# Revit family: IS_ConceptAir_Multiproduct_BIM_GB_E0817;E0818;E0819;E0821;E0842;E0844;E0846
name_source: partatom
category: Plumbing Fixtures
revit_build: Autodesk Revit MEP 2014 (Build: 20140709_2115(x64)
units: mm (PartAtom-declared; Revit-internal decimal feet)

## types (42) — shared parameters
Accessories = www.idealspec.co.uk
AreaUnits = millimeters
Assembly Code = C1030200
AssetType = Fixed
BREEAM = No
Brand = IdealStandard
Default Elevation = 800 mm  [stored 2.62467 ft]
DurationUnit = year
ECA = No
ExpectedLife = 30
IfcExportAs = IfcFurnitureType
IfcExportType = USERDEFINED
InstallationInstructions = www.idealspec.co.uk/resources.html
LinearUnits = millimeters
ManufacturerURL = www.idealspec.co.uk
Material = Laquered MDF
NBSDescription = Bathroom integrated duct work
NBSReference = 45-35-72/320
NettWeight = 0 Kg
Shape = Rectangular
Space = Internal
SpareParts = www.fastpart-spares.co.uk
TMV3 = No
URL = www.idealspec.co.uk
Uniclass2 = Pr_40_30_78_04
Version = 1
VolumeUnits = Litres
WRAS = No
WarrantyDescription = Manufacturers warranty
WarrantyDurationParts = 5
WarrantyDurationUnit = year
WaterEfficientProduct = No
zero-valued in all types: CWFU, Cost, HWFU, WFU

## per-type parameters (varying)
| type | 1Drawer | 2Drawer | BIMObjectName | Color | Description | Features | Finish | InnerColour | MainColor | MainColour | Model | ModelNumber | ModelReference | Name | NominalDepth | NominalHeight | NominalLength | NominalWidth | ProductInformation | Size |
| E0818B2 - 60CM Wall Hung Vanity Unit 2 drawers Gls White + Matt White | No | Yes | ISI_IdealStandard_Furniture_ConceptAir_E0818B2 | White | Concept Air 60 cm Wall Hung Vanity Unit 2 Drawers Gls White + Matt White | 60 cm Wall Hung Vanity Unit 2 Drawers Gls White + Matt White | White | ISI_IdealStandard_Laminate_White_Render | White | ISI_IdealStandard_Laminate_White_Render | E0818B2 | E0818B2 | Concept Air 60 cm Wall Hung Vanity Unit 2 Drawers Gls White + Matt White | Furniture_ConceptAir_E0818B2_IdealStandard | 440 mm  [stored 1.44357 ft] | 517 mm  [stored 1.69619 ft] | 440 mm  [stored 1.44357 ft] | 600 mm | www.idealspec.co.uk/assets/datasheet/E0818B2 | 517 x 440 x 600 mm |
| E0818EQ - 60CM Wall Hung Vanity Unit 2 drawers Gls Light Grey + Matt White | No | Yes | ISI_IdealStandard_Furniture_ConceptAir_E0818EQ | Grey | Concept Air 60 cm Wall Hung Vanity Unit 2 Drawers Gls Light Grey + Matt White | 60 cm Wall Hung Vanity Unit 2 Drawers Gls Light Grey + Matt White | Grey | ISI_IdealStandard_Laminate_White_Render | Grey | ISI_IdealStandard_Furniture_Grey_Render | E0818EQ | E0818EQ | Concept Air 60 cm Wall Hung Vanity Unit 2 Drawers Gls Light Grey + Matt White | Furniture_ConceptAir_E0818EQ_IdealStandard | 440 mm  [stored 1.44357 ft] | 517 mm  [stored 1.69619 ft] | 440 mm  [stored 1.44357 ft] | 600 mm | www.idealspec.co.uk/assets/datasheet/E0818EQ | 517 x 440 x 600 mm |
| E0818KN - 60CM Wall Hung Vanity Unit 2 drawers Gls White + Matt Light Grey | No | Yes | ISI_IdealStandard_Furniture_ConceptAir_E0818KN | White | Concept Air 60 cm Wall Hung Vanity Unit 2 Drawers Gls White + Matt Light Grey | 60 cm Wall Hung Vanity Unit 2 Drawers Gls White + Matt Light Grey | White | ISI_IdealStandard_Furniture_Grey_Render | White | ISI_IdealStandard_Laminate_White_Render | E0818KN | E0818KN | Concept Air 60 cm Wall Hung Vanity Unit 2 Drawers Gls White + Matt Light Grey | Furniture_ConceptAir_E0818KN_IdealStandard | 440 mm  [stored 1.44357 ft] | 517 mm  [stored 1.69619 ft] | 440 mm  [stored 1.44357 ft] | 600 mm | www.idealspec.co.uk/assets/datasheet/E0818KN | 517 x 440 x 600 mm |
| E0818PS - 60CM Wall Hung Vanity Unit 2 drawers Wood Light Grey + Matt White | No | Yes | ISI_IdealStandard_Furniture_ConceptAir_E0818PS | Wood grey | Concept Air 60 cm Wall Hung Vanity Unit 2 Drawers Wood Light Grey + Matt White | 60 cm Wall Hung Vanity Unit 2 Drawers Wood Light Grey + Matt White | Wood grey | ISI_IdealStandard_Laminate_White_Render | Wood grey | ISI_IdealStandard_Furniture_WoodLightGrey_Render | E0818PS | E0818PS | Concept Air 60 cm Wall Hung Vanity Unit 2 Drawers Wood Light Grey + Matt White | Furniture_ConceptAir_E0818PS_IdealStandard | 440 mm  [stored 1.44357 ft] | 517 mm  [stored 1.69619 ft] | 440 mm  [stored 1.44357 ft] | 600 mm | www.idealspec.co.uk/assets/datasheet/E0818PS | 517 x 440 x 600 mm |
| E0818UK - 60CM Wall Hung Vanity Unit 2 drawers Wood Light Brown + Matt Light Brown | No | Yes | ISI_IdealStandard_Furniture_ConceptAir_E0818UK | Wood brown | Concept Air 60 cm Wall Hung Vanity Unit 2 Drawers Wood Light Brown + Matt Light Brown | 60 cm Wall Hung Vanity Unit 2 Drawers Wood Light Brown + Matt Light Brown | Wood brown | ISI_IdealStandard_Furniture_WoodLightBrown_Render | Wood brown | ISI_IdealStandard_Furniture_WoodLightBrown_Render | E0818UK | E0818UK | Concept Air 60 cm Wall Hung Vanity Unit 2 Drawers Wood Light Brown + Matt Light Brown | Furniture_ConceptAir_E0818UK_IdealStandard | 440 mm  [stored 1.44357 ft] | 517 mm  [stored 1.69619 ft] | 440 mm  [stored 1.44357 ft] | 600 mm | www.idealspec.co.uk/assets/datasheet/E0818UK | 517 x 440 x 600 mm |
| E0819B2 - 80CM Wall Hung Vanity Unit 2 drawers Gls White + Matt White | No | Yes | ISI_IdealStandard_Furniture_ConceptAir_E0819B2 | White | Concept Air 80 cm Wall Hung Vanity Unit 2 Drawers Gls White + Matt White | 80 cm Wall Hung Vanity Unit 2 Drawers Gls White + Matt White | White | ISI_IdealStandard_Laminate_White_Render | White | ISI_IdealStandard_Laminate_White_Render | E0819B2 | E0819B2 | Concept Air 80 cm Wall Hung Vanity Unit 2 Drawers Gls White + Matt White | Furniture_ConceptAir_E0819B2_IdealStandard | 440 mm  [stored 1.44357 ft] | 517 mm  [stored 1.69619 ft] | 440 mm  [stored 1.44357 ft] | 800 mm  [stored 2.62467 ft] | www.idealspec.co.uk/assets/datasheet/E0819B2 | 517 x 440 x 800 mm |
| E0821EQ - 100CM Wall Hung Vanity Unit 2 drawers Gls Light Grey + Matt White | No | Yes | ISI_IdealStandard_Furniture_ConceptAir_E0821EQ | Grey | Concept Air 100 cm Wall Hung Vanity Unit 2 Drawers Gls Light Grey + Matt White | 100 cm Wall Hung Vanity Unit 2 Drawers Gls Light Grey + Matt White | Grey | ISI_IdealStandard_Laminate_White_Render | Grey | ISI_IdealStandard_Furniture_Grey_Render | E0821EQ | E0821EQ | Concept Air 100 cm Wall Hung Vanity Unit 2 Drawers Gls Light Grey + Matt White | Furniture_ConceptAir_E0821EQ_IdealStandard | 440 mm  [stored 1.44357 ft] | 517 mm  [stored 1.69619 ft] | 440 mm  [stored 1.44357 ft] | 1000 mm  [stored 3.28084 ft] | www.idealspec.co.uk/assets/datasheet/E0821EQ | 517 x 440 x 1000 mm |
| E0819KN - 80CM Wall Hung Vanity Unit 2 drawers Gls White + Matt Light Grey | No | Yes | ISI_IdealStandard_Furniture_ConceptAir_E0819KN | White | Concept Air 80 cm Wall Hung Vanity Unit 2 Drawers Gls White + Matt Light Grey | 80 cm Wall Hung Vanity Unit 2 Drawers Gls White + Matt Light Grey | White | ISI_IdealStandard_Furniture_Grey_Render | White | ISI_IdealStandard_Laminate_White_Render | E0819KN | E0819KN | Concept Air 80 cm Wall Hung Vanity Unit 2 Drawers Gls White + Matt Light Grey | Furniture_ConceptAir_E0819KN_IdealStandard | 440 mm  [stored 1.44357 ft] | 517 mm  [stored 1.69619 ft] | 440 mm  [stored 1.44357 ft] | 800 mm  [stored 2.62467 ft] | www.idealspec.co.uk/assets/datasheet/E0819KN | 517 x 440 x 800 mm |
| E0819PS - 80CM Wall Hung Vanity Unit 2 drawers Wood Light Grey + Matt White | No | Yes | ISI_IdealStandard_Furniture_ConceptAir_E0819PS | Wood grey | Concept Air 80 cm Wall Hung Vanity Unit 2 Drawers Wood Light Grey + Matt White | 80 cm Wall Hung Vanity Unit 2 Drawers Wood Light Grey + Matt White | Wood grey | ISI_IdealStandard_Laminate_White_Render | Wood grey | ISI_IdealStandard_Furniture_WoodLightGrey_Render | E0819PS | E0819PS | Concept Air 80 cm Wall Hung Vanity Unit 2 Drawers Wood Light Grey + Matt White | Furniture_ConceptAir_E0819PS_IdealStandard | 440 mm  [stored 1.44357 ft] | 517 mm  [stored 1.69619 ft] | 440 mm  [stored 1.44357 ft] | 800 mm  [stored 2.62467 ft] | www.idealspec.co.uk/assets/datasheet/E0819PS | 517 x 440 x 800 mm |
| E0819UK - 80CM Wall Hung Vanity Unit 2 drawers Wood Light Brown + Matt Light Brown | No | Yes | ISI_IdealStandard_Furniture_ConceptAir_E0819UK | Wood brown | Concept Air 80 cm Wall Hung Vanity Unit 2 Drawers Wood Light Brown + Matt Light Brown | 80 cm Wall Hung Vanity Unit 2 Drawers Wood Light Brown + Matt Light Brown | Wood brown | ISI_IdealStandard_Furniture_WoodLightBrown_Render | Wood brown | ISI_IdealStandard_Furniture_WoodLightBrown_Render | E0819UK | E0819UK | Concept Air 80 cm Wall Hung Vanity Unit 2 Drawers Wood Light Brown + Matt Light Brown | Furniture_ConceptAir_E0819UK_IdealStandard | 440 mm  [stored 1.44357 ft] | 517 mm  [stored 1.69619 ft] | 440 mm  [stored 1.44357 ft] | 800 mm  [stored 2.62467 ft] | www.idealspec.co.uk/assets/datasheet/E0819UK | 517 x 440 x 800 mm |
| E0819EQ - 80CM Wall Hung Vanity Unit 2 drawers Gls Light Grey + Matt White | No | Yes | ISI_IdealStandard_Furniture_ConceptAir_E0819EQ | Grey | Concept Air 80 cm Wall Hung Vanity Unit 2 Drawers Gls Light Grey + Matt White | 80 cm Wall Hung Vanity Unit 2 Drawers Gls Light Grey + Matt White | Grey | ISI_IdealStandard_Laminate_White_Render | Grey | ISI_IdealStandard_Furniture_Grey_Render | E0819EQ | E0819EQ | Concept Air 80 cm Wall Hung Vanity Unit 2 Drawers Gls Light Grey + Matt White | Furniture_ConceptAir_E0819EQ_IdealStandard | 440 mm  [stored 1.44357 ft] | 517 mm  [stored 1.69619 ft] | 440 mm  [stored 1.44357 ft] | 800 mm  [stored 2.62467 ft] | www.idealspec.co.uk/assets/datasheet/E0819EQ | 517 x 440 x 800 mm |
| E0821KN - 100CM Wall Hung Vanity Unit 2 drawers Gls White + Matt Light Grey | No | Yes | ISI_IdealStandard_Furniture_ConceptAir_E0821KN | White | Concept Air 100 cm Wall Hung Vanity Unit 2 Drawers Gls White + Matt Light Grey | 100 cm Wall Hung Vanity Unit 2 Drawers Gls White + Matt Light Grey | White | ISI_IdealStandard_Furniture_Grey_Render | White | ISI_IdealStandard_Laminate_White_Render | E0821KN | E0821KN | Concept Air 100 cm Wall Hung Vanity Unit 2 Drawers Gls White + Matt Light Grey | Furniture_ConceptAir_E0821KN_IdealStandard | 440 mm  [stored 1.44357 ft] | 517 mm  [stored 1.69619 ft] | 440 mm  [stored 1.44357 ft] | 1000 mm  [stored 3.28084 ft] | www.idealspec.co.uk/assets/datasheet/E0821KN | 517 x 440 x 1000 mm |
| E0821PS - 100CM Wall Hung Vanity Unit 2 drawers Wood Light Grey + Matt White | No | Yes | ISI_IdealStandard_Furniture_ConceptAir_E0821PS | Wood grey | Concept Air 100 cm Wall Hung Vanity Unit 2 Drawers Wood Light Grey + Matt White | 100 cm Wall Hung Vanity Unit 2 Drawers Wood Light Grey + Matt White | Wood grey | ISI_IdealStandard_Laminate_White_Render | Wood grey | ISI_IdealStandard_Furniture_WoodLightGrey_Render | E0821PS | E0821PS | Concept Air 100 cm Wall Hung Vanity Unit 2 Drawers Wood Light Grey + Matt White | Furniture_ConceptAir_E0821PS_IdealStandard | 440 mm  [stored 1.44357 ft] | 517 mm  [stored 1.69619 ft] | 440 mm  [stored 1.44357 ft] | 1000 mm  [stored 3.28084 ft] | www.idealspec.co.uk/assets/datasheet/E0821PS | 517 x 440 x 1000 mm |
| E0821UK - 100CM Wall Hung Vanity Unit 2 drawers Wood Light Brown + Matt Light Brown | No | Yes | ISI_IdealStandard_Furniture_ConceptAir_E0821UK | Wood brown | Concept Air 100 cm Wall Hung Vanity Unit 2 Drawers Wood Light Brown + Matt Light Brown | 100 cm Wall Hung Vanity Unit 2 Drawers Wood Light Brown + Matt Light Brown | Wood brown | ISI_IdealStandard_Furniture_WoodLightBrown_Render | Wood brown | ISI_IdealStandard_Furniture_WoodLightBrown_Render | E0821UK | E0821UK | Concept Air 100 cm Wall Hung Vanity Unit 2 Drawers Wood Light Brown + Matt Light Brown | Furniture_ConceptAir_E0821UK_IdealStandard | 440 mm  [stored 1.44357 ft] | 517 mm  [stored 1.69619 ft] | 440 mm  [stored 1.44357 ft] | 1000 mm  [stored 3.28084 ft] | www.idealspec.co.uk/assets/datasheet/E0821UK | 517 x 440 x 1000 mm |
| E0821B2 - 100CM Wall Hung Vanity Unit 2 drawers Gls White + Matt White | No | Yes | ISI_IdealStandard_Furniture_ConceptAir_E0821B2 | White | Concept Air 100 cm Wall Hung Vanity Unit 2 Drawers Gls White + Matt White | 100 cm Wall Hung Vanity Unit 2 Drawers Gls White + Matt White | White | ISI_IdealStandard_Laminate_White_Render | White | ISI_IdealStandard_Laminate_White_Render | E0821B2 | E0821B2 | Concept Air 100 cm Wall Hung Vanity Unit 2 Drawers Gls White + Matt White | Furniture_ConceptAir_E0821B2_IdealStandard | 440 mm  [stored 1.44357 ft] | 517 mm  [stored 1.69619 ft] | 440 mm  [stored 1.44357 ft] | 1000 mm  [stored 3.28084 ft] | www.idealspec.co.uk/assets/datasheet/E0821B2 | 517 x 440 x 1000 mm |
| E0817B2 - 50CM Wall Hung Vanity Unit 1 drawer Gls White + Matt White | Yes | No | ISI_IdealStandard_Furniture_ConceptAir_E0817B2 | White | Concept Air 50 cm Wall Hung Vanity Unit 1 Drawer Gls White + Matt White | 50 cm Wall Hung Vanity Unit 1 Drawer Gls White + Matt White | White | ISI_IdealStandard_Laminate_White_Render | White | ISI_IdealStandard_Laminate_White_Render | E0817B2 | E0817B2 | Concept Air 50 cm Wall Hung Vanity Unit 1 Drawer Gls White + Matt White | Furniture_ConceptAir_E0817B2_IdealStandard | 360 mm  [stored 1.1811 ft] | 400 mm  [stored 1.31234 ft] | 360 mm  [stored 1.1811 ft] | 500 mm  [stored 1.64042 ft] | www.idealspec.co.uk/assets/datasheet/E0817B2 | 400 x 360 x 500 mm |
| E0817EQ - 50CM Wall Hung Vanity Unit 1 drawer Gls Light Grey + Matt White | Yes | No | ISI_IdealStandard_Furniture_ConceptAir_E0817EQ | Grey | Concept Air 50 cm Wall Hung Vanity Unit 1 Drawer Gls Light Grey + Matt White | 50 cm Wall Hung Vanity Unit 1 Drawer Gls White + Matt White | Grey | ISI_IdealStandard_Laminate_White_Render | Grey | ISI_IdealStandard_Furniture_Grey_Render | E0817EQ | E0817EQ | Concept Air 50 cm Wall Hung Vanity Unit 1 Drawer Gls Light Grey + Matt White | Furniture_ConceptAir_E0817EQ_IdealStandard | 360 mm  [stored 1.1811 ft] | 400 mm  [stored 1.31234 ft] | 360 mm  [stored 1.1811 ft] | 500 mm  [stored 1.64042 ft] | www.idealspec.co.uk/assets/datasheet/E0817EQ | 400 x 360 x 500 mm |
| E0817KN - 50CM Wall Hung Vanity Unit 1 drawer Gls White + Matt Light Grey | Yes | No | ISI_IdealStandard_Furniture_ConceptAir_E0817KN | White | Concept Air 50 cm Wall Hung Vanity Unit 1 Drawer Gls White + Matt Light Grey | 50 cm Wall Hung Vanity Unit 1 Drawer Gls White + Matt White | White | ISI_IdealStandard_Furniture_Grey_Render | White | ISI_IdealStandard_Laminate_White_Render | E0817KN | E0817KN | Concept Air 50 cm Wall Hung Vanity Unit 1 Drawer Gls White + Matt Light Grey | Furniture_ConceptAir_E0817KN_IdealStandard | 360 mm  [stored 1.1811 ft] | 400 mm  [stored 1.31234 ft] | 360 mm  [stored 1.1811 ft] | 500 mm  [stored 1.64042 ft] | www.idealspec.co.uk/assets/datasheet/E0817KN | 400 x 360 x 500 mm |
| E0817PS - 50CM Wall Hung Vanity Unit 1 drawer Wood Light Grey + Matt White | Yes | No | ISI_IdealStandard_Furniture_ConceptAir_E0817PS | Wood grey | Concept Air 50 cm Wall Hung Vanity Unit 1 Drawer Wood Light Grey + Matt White | 50 cm Wall Hung Vanity Unit 1 Drawer Wood Light Grey + Matt White | Wood grey | ISI_IdealStandard_Laminate_White_Render | Wood grey | ISI_IdealStandard_Furniture_WoodLightGrey_Render | E0817PS | E0817PS | Concept Air 50 cm Wall Hung Vanity Unit 1 Drawer Wood Light Grey + Matt White | Furniture_ConceptAir_E0817PS_IdealStandard | 360 mm  [stored 1.1811 ft] | 400 mm  [stored 1.31234 ft] | 360 mm  [stored 1.1811 ft] | 500 mm  [stored 1.64042 ft] | www.idealspec.co.uk/assets/datasheet/E0817PS | 400 x 360 x 500 mm |
| E0817UK - 50CM Wall Hung Vanity Unit 1 drawer Wood Light Brown + Matt Light Brown | Yes | No | ISI_IdealStandard_Furniture_ConceptAir_E0817UK | Wood brown | Concept Air 50 cm Wall Hung Vanity Unit 1 Drawer Wood Light Brown + Matt Light Brown | 50 cm Wall Hung Vanity Unit 1 Drawer Wood Light Brown + Matt Light Brown | Wood brown | ISI_IdealStandard_Furniture_WoodLightBrown_Render | Wood brown | ISI_IdealStandard_Furniture_WoodLightBrown_Render | E0817UK | E0817UK | Concept Air 50 cm Wall Hung Vanity Unit 1 Drawer Wood Light Brown + Matt Light Brown | Furniture_ConceptAir_E0817UK_IdealStandard | 360 mm  [stored 1.1811 ft] | 400 mm  [stored 1.31234 ft] | 360 mm  [stored 1.1811 ft] | 500 mm  [stored 1.64042 ft] | www.idealspec.co.uk/assets/datasheet/E0817UK | 400 x 360 x 500 mm |
| E0842B2 - 44CM Cube WH Vanity unit 1 drawer Gls White + Matt White | Yes | No | ISI_IdealStandard_Furniture_ConceptAir_E0842B2 | White | Concept Air 50 cm Cube Wh Vanity Unit 1 Drawer Gls White + Matt White | 50 cm Cube Wh Vanity Unit 1 Drawer Gls White + Matt White | White | ISI_IdealStandard_Laminate_White_Render | White | ISI_IdealStandard_Laminate_White_Render | E0842B2 | E0842B2 | Concept Air 44 cm Cube Wh Vanity Unit 1 Drawer Gls White + Matt White | Furniture_ConceptAir_E0842B2_IdealStandard | 412 mm  [stored 1.35171 ft] | 400 mm  [stored 1.31234 ft] | 412 mm  [stored 1.35171 ft] | 435 mm  [stored 1.42717 ft] | www.idealspec.co.uk/assets/datasheet/E0842B2 | 400 x 412 x 435 mm |
| E0842EQ - 44CM Cube WH Vanity unit 1 drawer Gls Light Grey + Matt White | Yes | No | ISI_IdealStandard_Furniture_ConceptAir_E0842EQ | Grey | Concept Air 50 cm Cube Wh Vanity Unit 1 Drawer Gls Light Grey + Matt White | 50 cm Cube Wh Vanity Unit 1 Drawer Gls Light Grey + Matt White | Grey | ISI_IdealStandard_Laminate_White_Render | Grey | ISI_IdealStandard_Furniture_Grey_Render | E0842EQ | E0842EQ | Concept Air 44 cm Cube Wh Vanity Unit 1 Drawer Gls Light Grey + Matt White | Furniture_ConceptAir_E0842EQ_IdealStandard | 412 mm  [stored 1.35171 ft] | 400 mm  [stored 1.31234 ft] | 412 mm  [stored 1.35171 ft] | 435 mm  [stored 1.42717 ft] | www.idealspec.co.uk/assets/datasheet/E0842EQ | 400 x 412 x 435 mm |
| E0842KN - 44CM Cube WH Vanity unit 1 drawer Gls White + Matt Light Grey | Yes | No | ISI_IdealStandard_Furniture_ConceptAir_E0842KN | White | Concept Air 50 cm Cube Wh Vanity Unit 1 Drawer Gls White + Matt Light Grey | 50 cm Cube Wh Vanity Unit 1 Drawer Gls White + Matt Light Grey | White | ISI_IdealStandard_Furniture_Grey_Render | White | ISI_IdealStandard_Laminate_White_Render | E0842KN | E0842KN | Concept Air 44 cm Cube Wh Vanity Unit 1 Drawer Gls White + Matt Light Grey | Furniture_ConceptAir_E0842KN_IdealStandard | 412 mm  [stored 1.35171 ft] | 400 mm  [stored 1.31234 ft] | 412 mm  [stored 1.35171 ft] | 435 mm  [stored 1.42717 ft] | www.idealspec.co.uk/assets/datasheet/E0842KN | 400 x 412 x 435 mm |
| E0842PS - 44CM Cube WH Vanity unit 1 drawer Wood Light Grey + Matt White | Yes | No | ISI_IdealStandard_Furniture_ConceptAir_E0842PS | Wood grey | Concept Air 50 cm Cube Wh Vanity Unit 1 Drawer Wood Light Grey + Matt White | 50 cm Cube Wh Vanity Unit 1 Drawer Wood Light Grey + Matt White | Wood grey | ISI_IdealStandard_Laminate_White_Render | Wood grey | ISI_IdealStandard_Furniture_WoodLightGrey_Render | E0842PS | E0842PS | Concept Air 44 cm Cube Wh Vanity Unit 1 Drawer Wood Light Grey + Matt White | Furniture_ConceptAir_E0842PS_IdealStandard | 412 mm  [stored 1.35171 ft] | 400 mm  [stored 1.31234 ft] | 412 mm  [stored 1.35171 ft] | 435 mm  [stored 1.42717 ft] | www.idealspec.co.uk/assets/datasheet/E0842PS | 400 x 412 x 435 mm |
| E0842UK - 44CM Cube WH Vanity unit 1 drawer Wood Light Brown + Matt Light Brown | Yes | No | ISI_IdealStandard_Furniture_ConceptAir_E0842UK | Wood brown | Concept Air 50 cm Cube Wh Vanity Unit 1 Drawer Wood Light Brown + Matt Light Brown | 50 cm Cube Wh Vanity Unit 1 Drawer Wood Light Brown + Matt Light Brown | Wood brown | ISI_IdealStandard_Furniture_WoodLightBrown_Render | Wood brown | ISI_IdealStandard_Furniture_WoodLightBrown_Render | E0842UK | E0842UK | Concept Air 44 cm Cube Wh Vanity Unit 1 Drawer Wood Light Brown + Matt Light Brown | Furniture_ConceptAir_E0842UK_IdealStandard | 412 mm  [stored 1.35171 ft] | 400 mm  [stored 1.31234 ft] | 412 mm  [stored 1.35171 ft] | 435 mm  [stored 1.42717 ft] | www.idealspec.co.uk/assets/datasheet/E0842UK | 400 x 412 x 435 mm |
| E0844B2 - 48CM Cube WH Vanity unit 1 drawer Gls White + Matt White | Yes | No | ISI_IdealStandard_Furniture_ConceptAir_E0844B2 | White | Concept Air 55 cm Cube Wh Vanity Unit 1 Drawer Gls White + Matt White | 55 cm Cube Wh Vanity Unit 1 Drawer Gls White + Matt White | White | ISI_IdealStandard_Laminate_White_Render | White | ISI_IdealStandard_Laminate_White_Render | E0844B2 | E0844B2 | Concept Air 48 cm Cube Wh Vanity Unit 1 Drawer Gls White + Matt White | Furniture_ConceptAir_E0844B2_IdealStandard | 412 mm  [stored 1.35171 ft] | 400 mm  [stored 1.31234 ft] | 412 mm  [stored 1.35171 ft] | 485 mm  [stored 1.59121 ft] | www.idealspec.co.uk/assets/datasheet/E0844B2 | 400 x 412 x 485 mm |
| E0844EQ - 48CM Cube WH Vanity unit 1 drawer Gls Light Grey + Matt White | Yes | No | ISI_IdealStandard_Furniture_ConceptAir_E0844EQ | Grey | Concept Air 55 cm Cube Wh Vanity Unit 1 Drawer Gls Light Grey + Matt White | 55 cm Cube Wh Vanity Unit 1 Drawer Gls Light Grey + Matt White | Grey | ISI_IdealStandard_Laminate_White_Render | Grey | ISI_IdealStandard_Furniture_Grey_Render | E0844EQ | E0844EQ | Concept Air 48 cm Cube Wh Vanity Unit 1 Drawer Gls Light Grey + Matt White | Furniture_ConceptAir_E0844EQ_IdealStandard | 412 mm  [stored 1.35171 ft] | 400 mm  [stored 1.31234 ft] | 412 mm  [stored 1.35171 ft] | 485 mm  [stored 1.59121 ft] | www.idealspec.co.uk/assets/datasheet/E0844EQ | 400 x 412 x 485 mm |
| E0844KN - 48CM Cube WH Vanity unit 1 drawer Gls White + Matt Light Grey | Yes | No | ISI_IdealStandard_Furniture_ConceptAir_E0844KN | White | Concept Air 55 cm Cube Wh Vanity Unit 1 Drawer Gls White + Matt Light Grey | 55 cm Cube Wh Vanity Unit 1 Drawer Gls White + Matt Light Grey | White | ISI_IdealStandard_Furniture_Grey_Render | White | ISI_IdealStandard_Laminate_White_Render | E0844KN | E0844KN | Concept Air 48 cm Cube Wh Vanity Unit 1 Drawer Gls White + Matt Light Grey | Furniture_ConceptAir_E0844KN_IdealStandard | 412 mm  [stored 1.35171 ft] | 400 mm  [stored 1.31234 ft] | 412 mm  [stored 1.35171 ft] | 485 mm  [stored 1.59121 ft] | www.idealspec.co.uk/assets/datasheet/E0844KN | 400 x 412 x 485 mm |
| E0844PS - 48CM Cube WH Vanity unit 1 drawer Wood Light Grey + Matt White | Yes | No | ISI_IdealStandard_Furniture_ConceptAir_E0844PS | Wood grey | Concept Air 55 cm Cube Wh Vanity Unit 1 Drawer Wood Light Grey + Matt White | 55 cm Cube Wh Vanity Unit 1 Drawer Wood Light Grey + Matt White | Wood grey | ISI_IdealStandard_Laminate_White_Render | Wood grey | ISI_IdealStandard_Furniture_WoodLightGrey_Render | E0844PS | E0844PS | Concept Air 48 cm Cube Wh Vanity Unit 1 Drawer Wood Light Grey + Matt White | Furniture_ConceptAir_E0844PS_IdealStandard | 412 mm  [stored 1.35171 ft] | 400 mm  [stored 1.31234 ft] | 412 mm  [stored 1.35171 ft] | 485 mm  [stored 1.59121 ft] | www.idealspec.co.uk/assets/datasheet/E0844PS | 400 x 412 x 485 mm |
| E0844UK - 48CM Cube WH Vanity unit 1 drawer Wood Light Brown + Matt Light Brown | Yes | No | ISI_IdealStandard_Furniture_ConceptAir_E0844UK | Wood brown | Concept Air 55 cm Cube Wh Vanity Unit 1 Drawer Wood Light Brown + Matt Light Brown | 55 cm Cube Wh Vanity Unit 1 Drawer Wood Light Brown + Matt Light Brown | Wood brown | ISI_IdealStandard_Furniture_WoodLightBrown_Render | Wood brown | ISI_IdealStandard_Furniture_WoodLightBrown_Render | E0844UK | E0844UK | Concept Air 48 cm Cube Wh Vanity Unit 1 Drawer Wood Light Brown + Matt Light Brown | Furniture_ConceptAir_E0844UK_IdealStandard | 412 mm  [stored 1.35171 ft] | 400 mm  [stored 1.31234 ft] | 412 mm  [stored 1.35171 ft] | 485 mm  [stored 1.59121 ft] | www.idealspec.co.uk/assets/datasheet/E0844UK | 400 x 412 x 485 mm |
| E0846B2 - 54CM Cube WH Vanity unit 1 drawer Gls White + Matt White | Yes | No | ISI_IdealStandard_Furniture_ConceptAir_E0846B2 | White | Concept Air 60 cm Cube Wh Vanity Unit 1 Drawer Gls White + Matt White | 60 cm Cube Wh Vanity Unit 1 Drawer Gls White + Matt White | White | ISI_IdealStandard_Laminate_White_Render | White | ISI_IdealStandard_Laminate_White_Render | E0846B2 | E0846B2 | Concept Air 54 cm Cube Wh Vanity Unit 1 Drawer Gls White + Matt White | Furniture_ConceptAir_E0846B2_IdealStandard | 412 mm  [stored 1.35171 ft] | 400 mm  [stored 1.31234 ft] | 412 mm  [stored 1.35171 ft] | 535 mm  [stored 1.75525 ft] | www.idealspec.co.uk/assets/datasheet/E0846B2 | 400 x 412 x 535 mm |
| E0846EQ - 54CM Cube WH Vanity unit 1 drawer Gls Light Grey + Matt White | Yes | No | ISI_IdealStandard_Furniture_ConceptAir_E0846EQ | Grey | Concept Air 60 cm Cube Wh Vanity Unit 1 Drawer Gls Light Grey + Matt White | 60 cm Cube Wh Vanity Unit 1 Drawer Gls Light Grey + Matt White | Grey | ISI_IdealStandard_Laminate_White_Render | Grey | ISI_IdealStandard_Furniture_Grey_Render | E0846EQ | E0846EQ | Concept Air 54 cm Cube Wh Vanity Unit 1 Drawer Gls Light Grey + Matt White | Furniture_ConceptAir_E0846EQ_IdealStandard | 412 mm  [stored 1.35171 ft] | 400 mm  [stored 1.31234 ft] | 412 mm  [stored 1.35171 ft] | 535 mm  [stored 1.75525 ft] | www.idealspec.co.uk/assets/datasheet/E0846EQ | 400 x 412 x 535 mm |
| E0846KN - 54CM Cube WH Vanity unit 1 drawer Gls White + Matt Light Grey | Yes | No | ISI_IdealStandard_Furniture_ConceptAir_E0846KN | White | Concept Air 60 cm Cube Wh Vanity Unit 1 Drawer Gls White + Matt Light Grey | 60 cm Cube Wh Vanity Unit 1 Drawer Gls White + Matt Light Grey | White | ISI_IdealStandard_Furniture_Grey_Render | White | ISI_IdealStandard_Laminate_White_Render | E0846KN | E0846KN | Concept Air 54 cm Cube Wh Vanity Unit 1 Drawer Gls White + Matt Light Grey | Furniture_ConceptAir_E0846KN_IdealStandard | 412 mm  [stored 1.35171 ft] | 400 mm  [stored 1.31234 ft] | 412 mm  [stored 1.35171 ft] | 535 mm  [stored 1.75525 ft] | www.idealspec.co.uk/assets/datasheet/E0846KN | 400 x 412 x 535 mm |
| E0846PS - 54CM Cube WH Vanity unit 1 drawer Wood Light Grey + Matt White | Yes | No | ISI_IdealStandard_Furniture_ConceptAir_E0846PS | Wood grey | Concept Air 60 cm Cube Wh Vanity Unit 1 Drawer Wood Light Grey + Matt White | 60 cm Cube Wh Vanity Unit 1 Drawer Wood Light Grey + Matt White | Wood grey | ISI_IdealStandard_Laminate_White_Render | Wood grey | ISI_IdealStandard_Furniture_WoodLightGrey_Render | E0846PS | E0846PS | Concept Air 54 cm Cube Wh Vanity Unit 1 Drawer Wood Light Grey + Matt White | Furniture_ConceptAir_E0846PS_IdealStandard | 412 mm  [stored 1.35171 ft] | 400 mm  [stored 1.31234 ft] | 412 mm  [stored 1.35171 ft] | 535 mm  [stored 1.75525 ft] | www.idealspec.co.uk/assets/datasheet/E0846PS | 400 x 412 x 535 mm |
| E0846UK - 54CM Cube WH Vanity unit 1 drawer Wood Light Brown + Matt Light Brown | Yes | No | ISI_IdealStandard_Furniture_ConceptAir_E0846UK | Wood brown | Concept Air 60 cm Cube Wh Vanity Unit 1 Drawer Wood Light Brown + Matt Light Brown | 60 cm Cube Wh Vanity Unit 1 Drawer Wood Light Brown + Matt Light Brown | Wood brown | ISI_IdealStandard_Furniture_WoodLightBrown_Render | Wood brown | ISI_IdealStandard_Furniture_WoodLightBrown_Render | E0846UK | E0846UK | Concept Air 54 cm Cube Wh Vanity Unit 1 Drawer Wood Light Brown + Matt Light Brown | Furniture_ConceptAir_E0846UK_IdealStandard | 412 mm  [stored 1.35171 ft] | 400 mm  [stored 1.31234 ft] | 412 mm  [stored 1.35171 ft] | 535 mm  [stored 1.75525 ft] | www.idealspec.co.uk/assets/datasheet/E0846UK | 400 x 412 x 535 mm |
| E0846VY - 54CM Cube WH Vanity unit 1 drawer Matt Dark Brown + Matt White | Yes | No | ISI_IdealStandard_Furniture_ConceptAir_E0846VY | Dark brown | Concept Air 60 cm Cube Wh Vanity Unit 1 Drawer Matt Dark Brown + Matt White | 60 cm Cube Wh Vanity Unit 1 Drawer Matt Dark Brown + Matt White | Dark brown | ISI_IdealStandard_Laminate_White_Render | Dark brown | ISI_IdealStandard_Furniture_DarkBrown_Render | E0846VY | E0846VY | Concept Air 54 cm Cube Wh Vanity Unit 1 Drawer Gls Dark Brown + Matt White | Furniture_ConceptAir_E0846VY_IdealStandard | 412 mm  [stored 1.35171 ft] | 400 mm  [stored 1.31234 ft] | 412 mm  [stored 1.35171 ft] | 535 mm  [stored 1.75525 ft] | www.idealspec.co.uk/assets/datasheet/E0846VY | 400 x 412 x 535 mm |
| E0844VY - 48CM Cube WH Vanity unit 1 drawer Matt Dark Brown + Matt White | Yes | No | ISI_IdealStandard_Furniture_ConceptAir_E0844VY | Dark brown | Concept Air 55 cm Cube Wh Vanity Unit 1 Drawer Matt Dark Brown + Matt White | 55 cm Cube Wh Vanity Unit 1 Drawer Matt Dark Brown + Matt White | Dark brown | ISI_IdealStandard_Laminate_White_Render | Dark brown | ISI_IdealStandard_Furniture_DarkBrown_Render | E0844VY | E0844VY | Concept Air 48 cm Cube Wh Vanity Unit 1 Drawer Gls Dark Brown + Matt White | Furniture_ConceptAir_E0844VY_IdealStandard | 412 mm  [stored 1.35171 ft] | 400 mm  [stored 1.31234 ft] | 412 mm  [stored 1.35171 ft] | 485 mm  [stored 1.59121 ft] | www.idealspec.co.uk/assets/datasheet/E0844VY | 400 x 412 x 485 mm |
| E0842VY - 44CM Cube WH Vanity unit 1 drawer Matt Dark Brown + Matt White | Yes | No | ISI_IdealStandard_Furniture_ConceptAir_E0842VY | Dark brown | Concept Air 50 cm Cube Wh Vanity Unit 1 Drawer Matt Dark Brown + Matt White | 50 cm Cube Wh Vanity Unit 1 Drawer Matt Dark Brown + Matt White | Dark brown | ISI_IdealStandard_Laminate_White_Render | Dark brown | ISI_IdealStandard_Furniture_DarkBrown_Render | E0842VY | E0842VY | Concept Air 44 cm Cube Wh Vanity Unit 1 Drawer Gls Dark Brown + Matt White | Furniture_ConceptAir_E0842VY_IdealStandard | 412 mm  [stored 1.35171 ft] | 400 mm  [stored 1.31234 ft] | 412 mm  [stored 1.35171 ft] | 435 mm  [stored 1.42717 ft] | www.idealspec.co.uk/assets/datasheet/E0842VY | 400 x 412 x 435 mm |
| E0817VY - 50CM Wall Hung Vanity Unit 1 drawer Matt Dark Brown + Matt White | Yes | No | ISI_IdealStandard_Furniture_ConceptAir_E0817VY | Dark brown | Concept Air 50 cm Wall Hung Vanity Unit 1 Drawer Matt Dark Brown + Matt White | 50 cm Wall Hung Vanity Unit 1 Drawer Matt Dark Brown + Matt White | Dark brown | ISI_IdealStandard_Laminate_White_Render | Dark brown | ISI_IdealStandard_Furniture_DarkBrown_Render | E0817VY | E0817VY | Concept Air 50 cm Wall Hung Vanity Unit 1 Drawer Gls Dark Brown + Matt White | Furniture_ConceptAir_E0817VY_IdealStandard | 360 mm  [stored 1.1811 ft] | 400 mm  [stored 1.31234 ft] | 360 mm  [stored 1.1811 ft] | 500 mm  [stored 1.64042 ft] | www.idealspec.co.uk/assets/datasheet/E0817VY | 400 x 360 x 500 mm |
| E0821VY - 100CM Wall Hung Vanity Unit 2 drawers Matt Dark Brown + Matt White | No | Yes | ISI_IdealStandard_Furniture_ConceptAir_E0821VY | Dark brown | Concept Air 100 cm Wall Hung Vanity Unit 2 Drawers Matt Dark Brown + Matt White | 100 cm Wall Hung Vanity Unit 2 Drawers Matt Dark Brown + Matt White | Dark brown | ISI_IdealStandard_Laminate_White_Render | Dark brown | ISI_IdealStandard_Furniture_DarkBrown_Render | E0821VY | E0821VY | Concept Air 100 cm Wall Hung Vanity Unit 2 Drawers Gls Dark Brown + Matt White | Furniture_ConceptAir_E0821VY_IdealStandard | 440 mm  [stored 1.44357 ft] | 517 mm  [stored 1.69619 ft] | 440 mm  [stored 1.44357 ft] | 1000 mm  [stored 3.28084 ft] | www.idealspec.co.uk/assets/datasheet/E0821VY | 517 x 440 x 1000 mm |
| E0819VY - 80CM Wall Hung Vanity Unit 2 drawers Matt Dark Brown + Matt White | No | Yes | ISI_IdealStandard_Furniture_ConceptAir_E0819VY | Dark brown | Concept Air 80 cm Wall Hung Vanity Unit 2 Drawers Matt Dark Brown + Matt White | 80 cm Wall Hung Vanity Unit 2 Drawers Matt Dark Brown + Matt White | Dark brown | ISI_IdealStandard_Laminate_White_Render | Dark brown | ISI_IdealStandard_Furniture_DarkBrown_Render | E0819VY | E0819VY | Concept Air 80 cm Wall Hung Vanity Unit 2 Drawers Gls Dark Brown + Matt White | Furniture_ConceptAir_E0819VY_IdealStandard | 440 mm  [stored 1.44357 ft] | 517 mm  [stored 1.69619 ft] | 440 mm  [stored 1.44357 ft] | 800 mm  [stored 2.62467 ft] | www.idealspec.co.uk/assets/datasheet/E0819VY | 517 x 440 x 800 mm |
| E0818VY - 60CM Wall Hung Vanity Unit 2 drawers Matt Dark Brown + Matt White | No | Yes | ISI_IdealStandard_Furniture_ConceptAir_E0818VY | Dark brown | Concept Air 60 cm Wall Hung Vanity Unit 2 Drawers Matt Dark Brown + Matt White | 60 cm Wall Hung Vanity Unit 2 Drawers Matt Dark Brown + Matt White | Dark brown | ISI_IdealStandard_Laminate_White_Render | Dark brown | ISI_IdealStandard_Furniture_DarkBrown_Render | E0818VY | E0818VY | Concept Air 60 cm Wall Hung Vanity Unit 2 Drawers Gls Dark Brown + Matt White | Furniture_ConceptAir_E0818VY_IdealStandard | 440 mm  [stored 1.44357 ft] | 517 mm  [stored 1.69619 ft] | 440 mm  [stored 1.44357 ft] | 600 mm | www.idealspec.co.uk/assets/datasheet/E0818VY | 517 x 440 x 600 mm |

note: [stored X ft] marks values corroborated as IEEE doubles in the binary element streams (Revit-internal decimal feet)

## geometry (parser evidence)
native form markers: Sweep x2
no freeform markers — native parametric forms only
